# Revit family: HVAC_Air-Conditioning_Ice-Air_PTAC_RSNU
name_source: partatom
category: Mechanical Equipment
revit_build: Autodesk Revit 2015 (Build: 20140606_1530(x64)
units: mm (PartAtom-declared; Revit-internal decimal feet)

## types (8) — shared parameters
2-pipe Inlet Description = Water Inlet Connection
2-pipe Outlet Description = Water Outlet Connection
Aluminum Material = Aluminum - Ice_Air - White
BIMobject category = Air Conditioning
BIMobject category code = hvac-air-con
BIMobject main category = HVAC
BIMobject main category code = hvac
Brand url = http://www.ice-air.com
CFM Outside Air = 60 CFM
CFM X Outside Air = 110 CFM
Copper Material = Copper - Ice_Air - Orange
Date of publishing = 1/13/2014
Depth = 20.25 "
Description = RSNU – New Construction PTAC to provide superior new construction heating and cooling systems or to replace old installations.
Design country = United States
Edition number = 1
Height = 16.75 "
IFC Classification = Heat Exchanger
Manufacturer = Ice Air
Manufacturer country = United States
Manufacturer name = Ice Air
Masterformat 2014 Code = 23 00 00
Masterformat 2014 Description = Heating, Ventilating, and Air Conditioning (HVAC)
NBS Reference Code = 03-03
NBS Reference Description = Air Conditioning Units
OmniClass Code = 23-33 39 11
OmniClass Description = Air Conditioners
Opening Height = 16.5 "
Pipe Length = 10 "
Product Guid = 5129b412-607e-4f94-954e-bbef0b020033
Product SKU = rsnu
Product data url = https://bimobject.com
Product family = PTAC
Product group = RSNU
Product url = http://www.ice-air.com
QR code = http://bimobject.com
Steel Material = Steel - Ice_Air - Galvanized
Technical description = http://www.ice-air.com
UNSPSC Code = 40101701
URL = http://www.ice-air.com
Uniclass 1.4 Code = JU
Uniclass 1.4 Description = Ventilation and air conditioning systems
Uniclass 2.0 Code = PR-03-03
Uniclass 2.0 Description = Air Conditioning Units
Uniclass 2015 Code = EF_65_80
Uniclass 2015 Name = Air conditioning
Uniformat II Code = D3090
Uniformat II Description = Other HVAC Systems & Equipment
Vent Offset = 4 "
Weight Net (Kg) = 0
Width = 42 "
zero-valued in all types: Nominal height, Nominal width

## per-type parameters (varying)
| type | Amperage | CFM Room Air (High) | CFM Room Air (Low) | Electric Heater | Energy Efficiency Rating | Heating Capacity (Hot Water) | Heating Capacity (Steam) | Inlet/Outlet Connection | Opening Width | Total Cooling Capacity | Voltage | Voltage (Range) | Wattage | Weight | z Type |
| 5RSNU07 | 6 A | 380 CFM | 300 CFM | 1500 W | 12 | 16500 Btu/h | 18700 Btu/h | 0 " | 41.75 " | 7700 Btu/h | 115 V | 115 V | 642 W | 113.00 lb | 1 |
| 5RSNU09 | 7 A | 380 CFM | 300 CFM | 1500 W | 12 | 16500 Btu/h | 18700 Btu/h | 0 " | 40 " | 9700 Btu/h | 115 V | 115 V | 808 W | 117.00 lb | 2 |
| 5RSNU13 | 8 A | 400 CFM | 350 CFM | 1500 W | 11.4 | 16500 Btu/h | 18700 Btu/h | 0 " | 40 " | 12800 Btu/h | 115 V | 115 V | 1105 W | 124.00 lb | 3 |
| 8RSNU07 | 3 A | 380 CFM | 300 CFM | 1500 W | 12 | 16500 Btu/h | 18700 Btu/h | 0 " | 40 " | 7700 Btu/h | 230 V | 208 - 230 V | 642 W | 117.00 lb | 4 |
| 8RSNU09 | 4 A | 380 CFM | 300 CFM | 1500 W | 12 | 16500 Btu/h | 18700 Btu/h | 0 " | 40 " | 9700 Btu/h | 230 V | 208 - 230 V | 808 W | 117.00 lb | 5 |
| 8RSNU13 | 6 A | 400 CFM | 350 CFM | 3000 W | 11.4 | 16500 Btu/h | 18700 Btu/h | 0 " | 40 " | 12800 Btu/h | 230 V | 208 - 230 V | 1123 W | 124.00 lb | 6 |
| 8RSNU16 | 7 A | 450 CFM | 380 CFM | 3000 W | 10.5 | 19400 Btu/h | 20200 Btu/h | 0 " | 40 " | 14400 Btu/h | 230 V | 208 - 230 V | 1371 W | 132.00 lb | 7 |
| 8RSNU18 | 8 A | 540 CFM | 450 CFM | 3000 W | 10.3 | 19400 Btu/h | 20200 Btu/h | 0.5 " | 40 " | 16400 Btu/h | 230 V | 115 V | 1592 W | 141.00 lb | 8 |

note: column(s) folded — value = type name in every type: Model

## geometry (parser evidence)
native form markers: Sweep x20
no freeform markers — native parametric forms only
